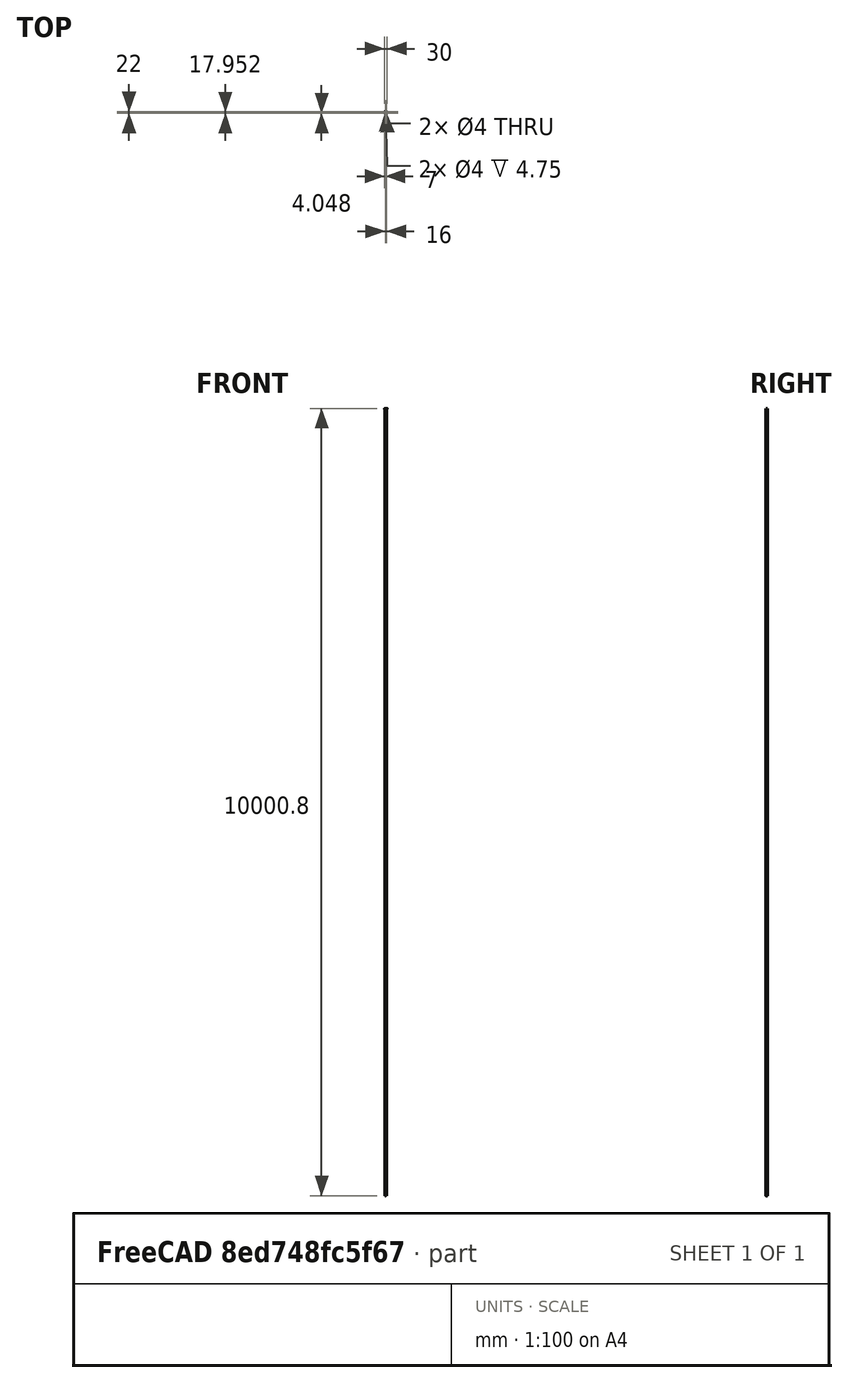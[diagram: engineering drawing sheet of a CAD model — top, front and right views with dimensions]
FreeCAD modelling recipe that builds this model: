
FCSTD DOCUMENT  (FreeCAD 0.16R5231 (Git))
Label: zCoupling
License: All rights reserved
LicenseURL: http://de.wikipedia.org/wiki/Alle_Rechte_vorbehalten
objects: Sketcher::SketchObject×5, PartDesign::Pocket×4, Part::Cylinder×2, Part::Fuse×2, Mesh::Feature×1, PartDesign::Pad×1, PartDesign::Fillet×1
note: 20 computed .brp shape members not serialized (recipe doc carries the construction recipe); baked Part::Feature solids carry a one-line shape summary decoded from their .brp

FEATURE [Mesh::Feature] z_coupling
  Placement = pos=(-17,11,0) rot=(0,0,1;0rad)
FEATURE [Sketcher::SketchObject] Sketch
  sketch-geometry (4):
    g0: LineSegment StartX=0 StartY=0 StartZ=0 EndX=30 EndY=0 EndZ=0
    g1: LineSegment StartX=30 StartY=0 StartZ=0 EndX=30 EndY=22 EndZ=0
    g2: LineSegment StartX=30 StartY=22 StartZ=0 EndX=0 EndY=22 EndZ=0
    g3: LineSegment StartX=0 StartY=22 StartZ=0 EndX=0 EndY=0 EndZ=0
  constraints (11):
    c: Coincident(g0,g1)
    c: Coincident(g1,g2)
    c: Coincident(g2,g3)
    c: Coincident(g3,g0)
    c: Horizontal(g0)
    c: Horizontal(g2)
    c: Vertical(g1)
    c: Vertical(g3)
    c: Coincident(g0,g-1)
    c: DistanceX(g2) = -30
    c: DistanceY(g1) = 22
FEATURE [PartDesign::Pad] Pad
  Length = 8
  Length2 = 100
  Sketch = -> Sketch
  Type = 0
FEATURE [Sketcher::SketchObject] Sketch001
  ExternalGeometry = -> [Pad]
  Placement = pos=(30,0,0) rot=(0.57735,0.57735,0.57735;2.0944rad)
  Support = -> Pad [Face2]
  sketch-geometry (3):
    g0: LineSegment [constr] StartX=11 StartY=8 StartZ=0 EndX=11 EndY=0 EndZ=0
    g1: ArcOfCircle CenterX=11 CenterY=8.75 CenterZ=0 NormalX=0 NormalY=0 NormalZ=1 Radius=3 StartAngle=3.14159 EndAngle=6.28319
    g2: LineSegment StartX=8 StartY=8.75 StartZ=0 EndX=14 EndY=8.75 EndZ=0
  constraints (11):
    c: PointOnObject(g0,g-3)
    c: PointOnObject(g0,g-4)
    c: Vertical(g0)
    c: Symmetric(g-4,g-4,g0)
    c: Radius(g1) = 3
    c: Coincident(g2,g1)
    c: Coincident(g2,g1)
    c: Horizontal(g2)
    c: PointOnObject(g1,g2)
    c: PointOnObject(g1,g0)
    c: DistanceY(g0,g1) = 0.75
FEATURE [PartDesign::Pocket] Pocket
  Length = 14
  Sketch = -> Sketch001
  Type = 0
FEATURE [Sketcher::SketchObject] Sketch002
  ExternalGeometry = -> [Pocket]
  Placement = pos=(0,0,0) rot=(0.57735,-0.57735,-0.57735;2.0944rad)
  Support = -> Pocket [Face2]
  sketch-geometry (3):
    g0: LineSegment [constr] StartX=-11 StartY=8 StartZ=0 EndX=-11 EndY=0 EndZ=0
    g1: ArcOfCircle CenterX=-11 CenterY=8.75 CenterZ=0 NormalX=0 NormalY=0 NormalZ=1 Radius=4 StartAngle=3.14159 EndAngle=6.28319
    g2: LineSegment StartX=-15 StartY=8.75 StartZ=0 EndX=-7 EndY=8.75 EndZ=0
  constraints (11):
    c: PointOnObject(g0,g-3)
    c: PointOnObject(g0,g-4)
    c: Vertical(g0)
    c: Symmetric(g-4,g-4,g0)
    c: Radius(g1) = 4
    c: Coincident(g2,g1)
    c: Coincident(g2,g1)
    c: Horizontal(g2)
    c: PointOnObject(g1,g2)
    c: PointOnObject(g1,g0)
    c: DistanceY(g1,g0) = -0.75
FEATURE [PartDesign::Pocket] Pocket001
  Length = 14
  Sketch = -> Sketch002
  Type = 0
FEATURE [Sketcher::SketchObject] Sketch003
  ExternalGeometry = -> [Pocket001]
  Placement = pos=(0,0,8) rot=(0,0,1;0rad)
  Support = -> Pocket001 [Face5]
  sketch-geometry (10):
    g0: LineSegment [constr] StartX=7 StartY=14.9291 StartZ=0 EndX=7 EndY=22 EndZ=0
    g1: LineSegment [constr] StartX=7 StartY=7.07094 StartZ=0 EndX=7 EndY=0 EndZ=0
    g2: LineSegment [constr] StartX=23 StartY=8.09526 StartZ=0 EndX=23 EndY=0 EndZ=0
    g3: LineSegment [constr] StartX=23 StartY=13.9047 StartZ=0 EndX=23 EndY=22 EndZ=0
    g4: LineSegment [constr] StartX=7 StartY=17.9524 StartZ=0 EndX=23 EndY=17.9524 EndZ=0
    g5: LineSegment [constr] StartX=7 StartY=4.04763 StartZ=0 EndX=23 EndY=4.04763 EndZ=0
    g6: Circle CenterX=7 CenterY=17.9524 CenterZ=0 NormalX=0 NormalY=0 NormalZ=1 Radius=2
    g7: Circle CenterX=23 CenterY=17.9524 CenterZ=0 NormalX=0 NormalY=0 NormalZ=1 Radius=2
    g8: Circle CenterX=7 CenterY=4.04763 CenterZ=0 NormalX=0 NormalY=0 NormalZ=1 Radius=2
    g9: Circle CenterX=23 CenterY=4.04763 CenterZ=0 NormalX=0 NormalY=0 NormalZ=1 Radius=2
  constraints (28):
    c: Vertical(g0)
    c: Vertical(g1)
    c: Vertical(g2)
    c: Vertical(g3)
    c: PointOnObject(g4,g0)
    c: PointOnObject(g4,g3)
    c: Horizontal(g4)
    c: PointOnObject(g5,g1)
    c: PointOnObject(g5,g2)
    c: Horizontal(g5)
    c: Coincident(g6,g4)
    c: Coincident(g7,g4)
    c: Coincident(g8,g5)
    c: Coincident(g9,g5)
    c: Equal(g6,g7)
    c: Equal(g7,g8)
    c: Equal(g8,g9)
    c: Radius(g6) = 2
    c: Symmetric(g3,g3,g4)
    c: Symmetric(g2,g2,g5)
    c: PointOnObject(g0,g-3)
    c: Symmetric(g-6,g-6,g0)
    c: PointOnObject(g3,g-3)
    c: Symmetric(g-7,g-7,g3)
    c: Symmetric(g-8,g-8,g2)
    c: PointOnObject(g2,g-4)
    c: Symmetric(g-5,g-5,g1)
    c: PointOnObject(g1,g-4)
FEATURE [PartDesign::Pocket] Pocket002
  Length = 5
  Sketch = -> Sketch003
  Type = 1
FEATURE [Sketcher::SketchObject] Sketch004
  ExternalGeometry = -> [Pocket002]
  Placement = pos=(0,0,0) rot=(1,0,0;3.14159rad)
  Support = -> Pocket002 [Face4]
  sketch-geometry (14):
    g0: LineSegment StartX=3.75 StartY=-17.9524 StartZ=0 EndX=5.375 EndY=-15.1378 EndZ=0
    g1: LineSegment StartX=5.375 StartY=-15.1378 StartZ=0 EndX=8.625 EndY=-15.1378 EndZ=0
    g2: LineSegment StartX=8.625 StartY=-15.1378 StartZ=0 EndX=10.25 EndY=-17.9524 EndZ=0
    g3: LineSegment StartX=10.25 StartY=-17.9524 StartZ=0 EndX=8.625 EndY=-20.767 EndZ=0
    g4: LineSegment StartX=8.625 StartY=-20.767 StartZ=0 EndX=5.375 EndY=-20.767 EndZ=0
    g5: LineSegment StartX=5.375 StartY=-20.767 StartZ=0 EndX=3.75 EndY=-17.9524 EndZ=0
    g6: LineSegment StartX=24.625 StartY=-15.1378 StartZ=0 EndX=21.375 EndY=-15.1378 EndZ=0
    g7: LineSegment StartX=21.375 StartY=-15.1378 StartZ=0 EndX=19.75 EndY=-17.9524 EndZ=0
    g8: LineSegment StartX=19.75 StartY=-17.9524 StartZ=0 EndX=21.375 EndY=-20.767 EndZ=0
    g9: LineSegment StartX=21.375 StartY=-20.767 StartZ=0 EndX=24.625 EndY=-20.767 EndZ=0
    g10: LineSegment StartX=24.625 StartY=-20.767 StartZ=0 EndX=26.25 EndY=-17.9524 EndZ=0
    g11: LineSegment StartX=26.25 StartY=-17.9524 StartZ=0 EndX=24.625 EndY=-15.1378 EndZ=0
    g12: LineSegment [constr] StartX=3.75 StartY=-17.9524 StartZ=0 EndX=10.25 EndY=-17.9524 EndZ=0
    g13: LineSegment [constr] StartX=19.75 StartY=-17.9524 StartZ=0 EndX=26.25 EndY=-17.9524 EndZ=0
  constraints (38):
    c: Coincident(g0,g1)
    c: Horizontal(g1)
    c: Coincident(g1,g2)
    c: Coincident(g2,g3)
    c: Coincident(g3,g4)
    c: Horizontal(g4)
    c: Coincident(g4,g5)
    c: Coincident(g5,g0)
    c: Horizontal(g6)
    c: Coincident(g6,g7)
    c: Coincident(g7,g8)
    c: Coincident(g8,g9)
    c: Horizontal(g9)
    c: Coincident(g9,g10)
    c: Coincident(g10,g11)
    c: Coincident(g11,g6)
    c: Coincident(g12,g0)
    c: Coincident(g12,g2)
    c: Horizontal(g12)
    c: Coincident(g13,g7)
    c: Coincident(g13,g10)
    c: Horizontal(g13)
    c: Equal(g12,g13)
    c: DistanceX(g12) = 6.5
    c: Equal(g0,g1)
    c: Equal(g1,g2)
    c: Equal(g2,g3)
    c: Equal(g3,g4)
    c: Equal(g4,g5)
    c: Equal(g11,g6)
    c: Equal(g6,g7)
    c: Equal(g7,g8)
    c: Equal(g8,g9)
    c: Equal(g9,g10)
    c: Angle(g1,g2) = 2.0944
    c: Angle(g6,g11) = 2.0944
    c: Symmetric(g12,g12,g-3)
    c: Symmetric(g13,g13,g-4)
FEATURE [PartDesign::Pocket] Pocket003
  Length = 3
  Sketch = -> Sketch004
  Type = 0
FEATURE [Part::Cylinder] Cylinder  label="Zylinder"
  Angle = 360
  Height = 0.25
  Placement = pos=(23,17.9524,3) rot=(0,0,1;0rad)
  Radius = 2
FEATURE [Part::Cylinder] Cylinder001  label="Zylinder001"
  Angle = 360
  Height = 0.25
  Placement = pos=(7,17.9524,3) rot=(0,0,1;0rad)
  Radius = 2
FEATURE [Part::Fuse] Fusion
  Base = -> Cylinder
  Tool = -> Cylinder001
FEATURE [PartDesign::Fillet] Fillet
  Base = -> Pocket003 [Edge9,Edge11,Edge2,Edge1]
  Radius = 5
FEATURE [Part::Fuse] Fusion001
  Base = -> Fusion
  Tool = -> Fillet
